SOLIDWORKS PART (.sldprt)
format: sldprt  version: not decoded by parser v0  size: 102,912 bytes
history: native  units: mm
features: plane x3, sketch x3, cut_extrude x2, material x1, extrude x1 (+9 scaffold rows collapsed)
feature tree (19):
  scaffold x9  (default folders/planes/origin — collapsed)
  material  "Matériau <non spécifié>"
  plane  "Plane1"
  plane  "Plane2"
  plane  "Plane3"
  sketch  "Esquisse5"  dims[D1=1.1mm]
  extrude  "Extrusion1"  Depth=6mm
  sketch  "Esquisse4"  dims[D1=4.1mm]
  cut_extrude  "Enlèv. mat.-Extru.2"  Depth=2.8mm
  sketch  "Esquisse6"  dims[D1=~2.313034mm]
  cut_extrude  "Enlèv. mat.-Extru.3"  Depth=2.5mm
decode coverage: 6 of 6 modeling features carry decoded parameters
note: ~ marks probable driven/reference dimensions
note: suppression state not decoded; provenance and decode notes live in map.json
